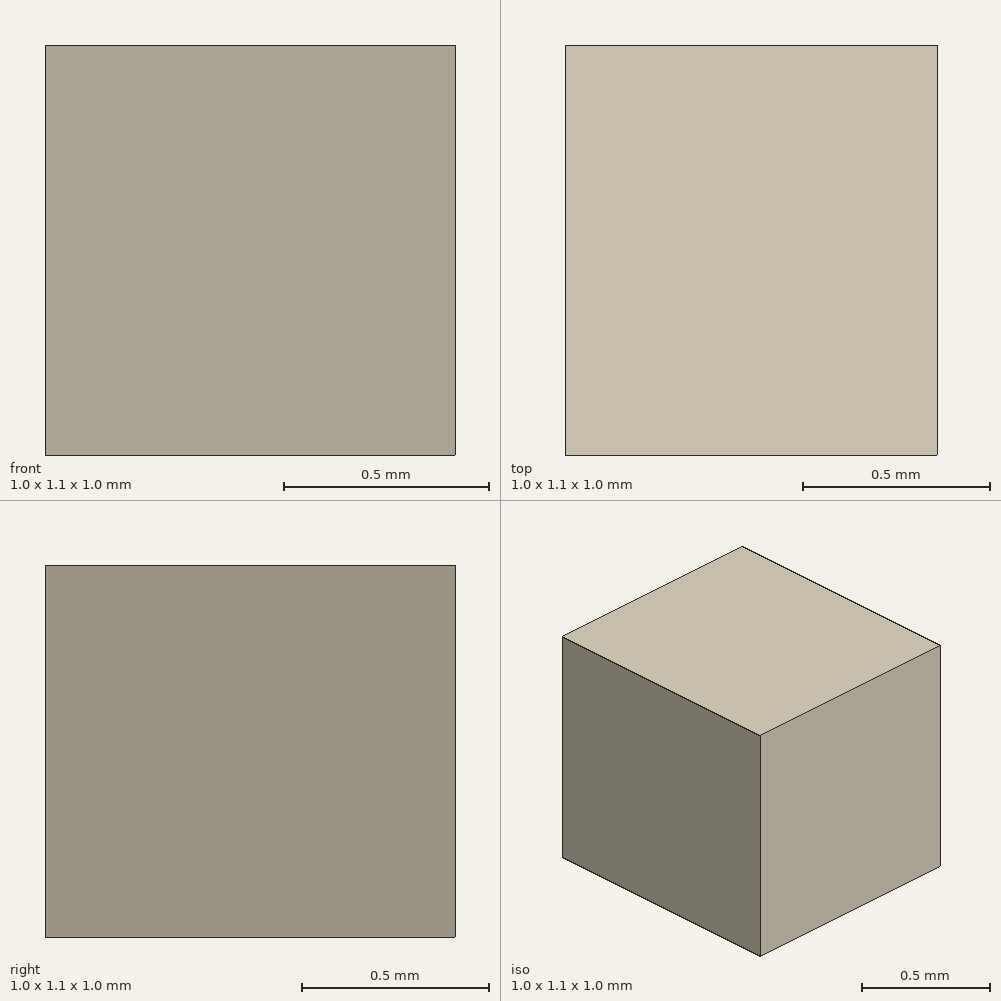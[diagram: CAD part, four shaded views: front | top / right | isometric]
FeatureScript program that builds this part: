
annotation { "Feature Type Name" : "Feature", "Feature Type Description" : "" }
export const myFeature = defineFeature(function(context is Context, id is Id, definition is map)
    precondition{}
    {
        {
            var Q0;
            Q0=qCreatedBy(makeId("Front.planeOp"),FACE);
            cPlane(context, id + "F0", {"entities" : qUnion([Q0]), "cplaneType" : CPlaneType.OFFSET, "offset" : 14 * mm, "oppositeDirection" : true, "width" : 150 * mm, "height" : 150 * mm});
        }
        {
            var Q0;
            Q0=qCreatedBy(id+"F0.planeOp",FACE);
            var sketch = newSketch(context, id + "F1", { "sketchPlane" : qUnion([Q0])});
            skPoint(sketch, "E0", {"position": v(145.09, 61.18) * mm});
            skLineSegment(sketch, "E1.bottom", {"start": v(145.09, 61.18) * mm, "end": v(146.09, 61.18) * mm});
            skLineSegment(sketch, "E1.top", {"start": v(145.09, 60.18) * mm, "end": v(146.09, 60.18) * mm});
            skLineSegment(sketch, "E1.left", {"start": v(145.09, 61.18) * mm, "end": v(145.09, 60.18) * mm});
            skLineSegment(sketch, "E1.right", {"start": v(146.09, 61.18) * mm, "end": v(146.09, 60.18) * mm});
            skSolve(sketch);
        }
        {
            var Q0;
            Q0=makeQuery(id+"F1.imprint","IMPRINT",FACE,{"disambiguationData":[TD([[makeQuery(id+"F1.imprint","IMPRINT",EDGE,{"derivedFrom":sQuery(id+"F1.wireOp",EDGE,"E1.bottom")}),-1.0]])]});
            extrude(context, id + "F2", {"entities" : qUnion([Q0]), "depth" : 1.1 * mm});
        }
    });
